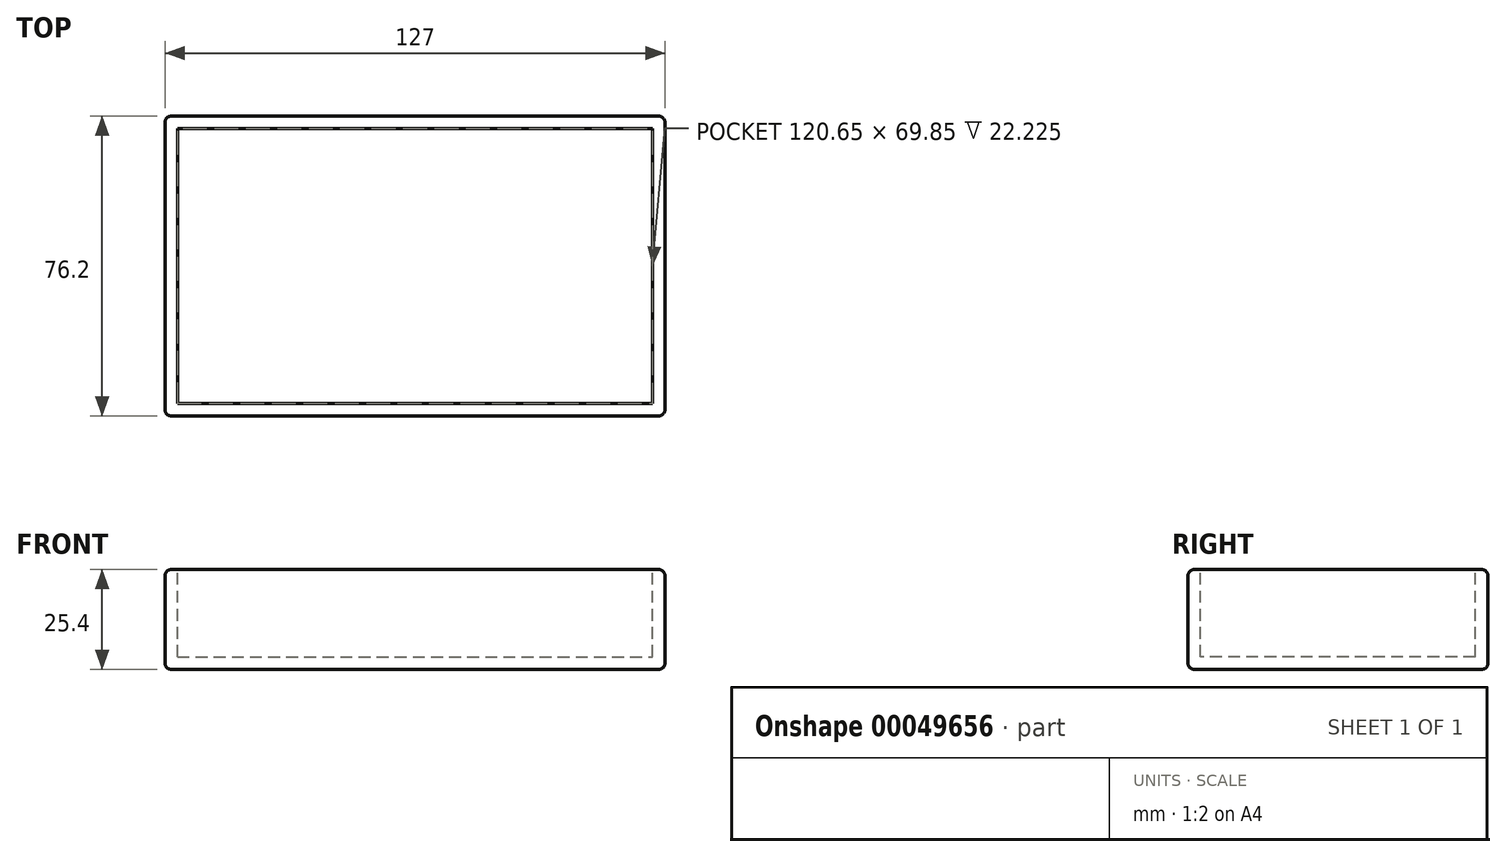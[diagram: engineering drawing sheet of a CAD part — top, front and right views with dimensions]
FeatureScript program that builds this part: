
annotation { "Feature Type Name" : "Feature", "Feature Type Description" : "" }
export const myFeature = defineFeature(function(context is Context, id is Id, definition is map)
    precondition{}
    {
        {
            var Q0;
            Q0=qCreatedBy(makeId("Top.planeOp"),FACE);
            var sketch = newSketch(context, id + "F0", { "sketchPlane" : qUnion([Q0])});
            skLineSegment(sketch, "E0.bottom", {"start": v(-57.13, 40.9) * mm, "end": v(69.87, 40.9) * mm});
            skLineSegment(sketch, "E0.top", {"start": v(-57.13, -35.3) * mm, "end": v(69.87, -35.3) * mm});
            skLineSegment(sketch, "E0.left", {"start": v(-57.13, 40.9) * mm, "end": v(-57.13, -35.3) * mm});
            skLineSegment(sketch, "E0.right", {"start": v(69.87, 40.9) * mm, "end": v(69.87, -35.3) * mm});
            skSolve(sketch);
        }
        {
            var Q0;
            Q0 = qSketchRegion(id + "F0", true);
            extrude(context, id + "F1", {"entities" : qUnion([Q0]), "oppositeDirection" : true, "depth" : 25.4 * mm});
        }
        {
            var Q0;
            Q0=makeQuery(id+"F1.opExtrude","CAP_FACE",FACE,{"disambiguationData":[OSD([sQuery(id+"F0.wireOp",EDGE,"E0.bottom"),sQuery(id+"F0.wireOp",EDGE,"E0.top"),sQuery(id+"F0.wireOp",EDGE,"E0.left"),sQuery(id+"F0.wireOp",EDGE,"E0.right")])],"isStart":true});
            var sketch = newSketch(context, id + "F2", { "sketchPlane" : qUnion([Q0])});
            skLineSegment(sketch, "E1.bottom", {"start": v(-53.96, 37.73) * mm, "end": v(66.7, 37.73) * mm});
            skLineSegment(sketch, "E1.top", {"start": v(-53.96, -32.12) * mm, "end": v(66.7, -32.12) * mm});
            skLineSegment(sketch, "E1.left", {"start": v(-53.96, 37.73) * mm, "end": v(-53.96, -32.12) * mm});
            skLineSegment(sketch, "E1.right", {"start": v(66.7, 37.73) * mm, "end": v(66.7, -32.12) * mm});
            skLineSegment(sketch, "E2", {"start": v(6.37, 37.73) * mm, "end": v(6.37, 40.9) * mm, "construction": true});
            skLineSegment(sketch, "E3", {"start": v(-53.96, 2.8) * mm, "end": v(-57.13, 2.8) * mm, "construction": true});
            skLineSegment(sketch, "E4", {"start": v(66.7, 2.8) * mm, "end": v(69.87, 2.8) * mm, "construction": true});
            skLineSegment(sketch, "E5", {"start": v(6.37, -32.12) * mm, "end": v(6.37, -35.3) * mm, "construction": true});
            skSolve(sketch);
        }
        {
            var Q0;
            Q0 = qSketchRegion(id + "F2", true);
            extrude(context, id + "F3", {"entities" : qUnion([Q0]), "operationType" : NewBodyOperationType.REMOVE, "oppositeDirection" : true, "depth" : 22.22 * mm});
        }
        {
            var Q0;
            Q0=makeQuery(id+"F1.opExtrude","CAP_EDGE",EDGE,{"disambiguationData":[OSD([sQuery(id+"F0.wireOp",EDGE,"E0.left")])],"isStart":true});
            var Q1;
            Q1=makeQuery(id+"F1.opExtrude","CAP_EDGE",EDGE,{"disambiguationData":[OSD([sQuery(id+"F0.wireOp",EDGE,"E0.top")])],"isStart":true});
            var Q2;
            Q2=makeQuery(id+"F1.opExtrude","CAP_EDGE",EDGE,{"disambiguationData":[OSD([sQuery(id+"F0.wireOp",EDGE,"E0.right")])],"isStart":true});
            var Q3;
            Q3=makeQuery(id+"F1.opExtrude","CAP_EDGE",EDGE,{"disambiguationData":[OSD([sQuery(id+"F0.wireOp",EDGE,"E0.bottom")])],"isStart":true});
            var Q4;
            Q4=makeQuery(id+"F3.boolean.opBoolean","COPY",EDGE,{"derivedFrom":makeQuery(id+"F3.opExtrude","CAP_EDGE",EDGE,{"disambiguationData":[OSD([sQuery(id+"F2.wireOp",EDGE,"E1.bottom")])],"isStart":true})});
            var Q5;
            Q5=makeQuery(id+"F3.boolean.opBoolean","COPY",EDGE,{"derivedFrom":makeQuery(id+"F3.opExtrude","CAP_EDGE",EDGE,{"disambiguationData":[OSD([sQuery(id+"F2.wireOp",EDGE,"E1.left")])],"isStart":true})});
            var Q6;
            Q6=makeQuery(id+"F3.boolean.opBoolean","COPY",EDGE,{"derivedFrom":makeQuery(id+"F3.opExtrude","CAP_EDGE",EDGE,{"disambiguationData":[OSD([sQuery(id+"F2.wireOp",EDGE,"E1.top")])],"isStart":true})});
            var Q7;
            Q7=makeQuery(id+"F3.boolean.opBoolean","COPY",EDGE,{"derivedFrom":makeQuery(id+"F3.opExtrude","CAP_EDGE",EDGE,{"disambiguationData":[OSD([sQuery(id+"F2.wireOp",EDGE,"E1.right")])],"isStart":true})});
            var Q8;
            Q8=makeQuery(id+"F1.opExtrude","SWEPT_EDGE",EDGE,{"disambiguationData":[OSD([sQuery(id+"F0.wireOp",EDGE,"E0.top"),sQuery(id+"F0.wireOp",EDGE,"E0.right")])]});
            var Q9;
            Q9=makeQuery(id+"F1.opExtrude","SWEPT_EDGE",EDGE,{"disambiguationData":[OSD([sQuery(id+"F0.wireOp",EDGE,"E0.top"),sQuery(id+"F0.wireOp",EDGE,"E0.left")])]});
            var Q10;
            Q10=makeQuery(id+"F1.opExtrude","CAP_EDGE",EDGE,{"disambiguationData":[OSD([sQuery(id+"F0.wireOp",EDGE,"E0.top")])],"isStart":false});
            var Q11;
            Q11=makeQuery(id+"F1.opExtrude","CAP_EDGE",EDGE,{"disambiguationData":[OSD([sQuery(id+"F0.wireOp",EDGE,"E0.right")])],"isStart":false});
            var Q12;
            Q12=makeQuery(id+"F1.opExtrude","SWEPT_EDGE",EDGE,{"disambiguationData":[OSD([sQuery(id+"F0.wireOp",EDGE,"E0.bottom"),sQuery(id+"F0.wireOp",EDGE,"E0.right")])]});
            var Q13;
            Q13=makeQuery(id+"F1.opExtrude","SWEPT_EDGE",EDGE,{"disambiguationData":[OSD([sQuery(id+"F0.wireOp",EDGE,"E0.bottom"),sQuery(id+"F0.wireOp",EDGE,"E0.left")])]});
            var Q14;
            Q14=makeQuery(id+"F1.opExtrude","CAP_EDGE",EDGE,{"disambiguationData":[OSD([sQuery(id+"F0.wireOp",EDGE,"E0.bottom")])],"isStart":false});
            var Q15;
            Q15=makeQuery(id+"F1.opExtrude","CAP_EDGE",EDGE,{"disambiguationData":[OSD([sQuery(id+"F0.wireOp",EDGE,"E0.left")])],"isStart":false});
            fillet(context, id + "F4", {"entities" : qUnion([Q0, Q1, Q2, Q3, Q4, Q5, Q6, Q7, Q8, Q9, Q10, Q11, Q12, Q13, Q14, Q15]), "radius" : 1.57 * mm, "tangentPropagation" : true, "allowEdgeOverflow" : false});
        }
    });
